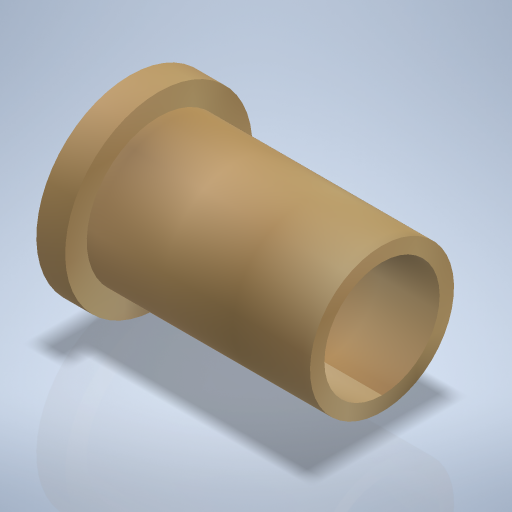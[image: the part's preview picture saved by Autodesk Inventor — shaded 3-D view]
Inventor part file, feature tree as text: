
AUTODESK INVENTOR PART (.ipt)
format: ipt  version: 2024 (Build 280153000, 153)  size: 284,672 bytes
history: native  units: mm
features: sketch x2, revolve x1, hole x1
ambient origin geometry x8: Origin, YZ Plane, XZ Plane, XY Plane, X Axis, Y Axis, Z Axis, Center Point
bodies: Volumenkörper1 (feature_tree)
feature tree (4):
  revolve  "Umdrehung1"
  hole  "Bohrung1"  [1 undecoded]
  sketch  "Skizze1"  dims[d0=10.0mm d1=13.0mm]
  sketch  "Skizze2"  dims[d2=2.0mm d3=15.5mm d4=90.0deg d5=8.0mm d6=6.0mm d7=4.0mm d8=2.0mm d9=90.0deg d10=8.0mm d11=20.594885mm]
note: 1 required parameter value undecoded (feature->parameter linkage not recoverable at this tier; creation-order binding heuristic only, values carry confidence <= 0.55)
